# Revit family: IS_Douro_R3806_BIM_NL
name_source: partatom
category: Plumbing Fixtures
revit_build: Autodesk Revit MEP 2014 (Build: 20130308_1515(x64)
units: mm (PartAtom-declared; Revit-internal decimal feet)

## types (1)
- R380601 - DUORO UITGIETBAK WIT
    Accessories = www.idealstandardnederland.nl
    AreaUnits = millimeters
    Assembly Code = C1030200
    AssetType = Vast
    BIMObjectName = ISI_IdealStandard_JanitorialSinks_R380601
    BarCode = 3139000034436
    Brand = Ideal Standard
    CWFU = 0
    Color = Wit
    ConnectionType = Sanitair
    Cost = 0 $
    Default Elevation = 803 mm  [stored 2.63451 ft]
    Description = Contour 21 / Douro uitgietbak 445 mm van keramiek met stootrand. Te monteren met rooster (R6378AA). Rooster en bevestigingsset separaat te bestellen.
    DrainSize = 0 mm  [stored 0 ft]
    DurationUnit = jaar
    ECA = No
    ExpectedLife = 25
    Features = Uitgietbak 445 mm van keramiek met stootrand. Te monteren met rooster (R6378AA). Rooster en bevestigingsset separaat te bestellen.
    Finish = Wit
    HWFU = 0
    IfcExportAs = IfcSanitaryTerminalType
    IfcExportType = SINK
    InstallationInstructions = http://www.idealstandardnederland.nl
    LinearUnits = millimeters
    ManufacturerURL = www.idealstandardnederland.nl
    Material = Keramiek
    MetalFinish = ASH_ArmitageShanks_StainlessSteel_Silver_Render
    Model = R380601
    ModelNumber = R380601
    ModelReference = Contour 21 / Douro uitgietbak 445 mm van keramiek met stootrand. Te monteren met rooster (R6378AA). Rooster en bevestigingsset separaat te bestellen.
    NBSDescription = Janitorial units
    NBSReference = 45-35-70/401
    Name = JanitorialSinks_R380601_IdealStandard
    NettWeight = 17.204 kg
    NominalDepth = 0 mm  [stored 0 ft]
    NominalHeight = 345 mm  [stored 1.13189 ft]
    NominalLength = 354 mm
    NominalWidth = 445 mm
    ProductInformation = http://www.idealstandardnederland.nl
    Shape = Gesculptuurd
    SinkMounting = Wall
    SinkType = Other
    Size = 445 x 354 x 345 mm
    Space = Internal
    URL = www.idealstandardnederland.nl
    Uniclass2015Code = Pr_40_20_96_44
    Uniclass2015Title = Janitorial sinks
    Uniclass2015Version = Products v1.1
    Version = 1
    VolumeUnits = liter
    WFU = 0
    WRAS = No
    WarrantyDescription = Fabrieksgarantie
    WarrantyDurationParts = 5
    WarrantyDurationUnit = jaar
    WaterEfficientProduct = No

note: [stored X ft] marks values corroborated as IEEE doubles in the binary element streams (Revit-internal decimal feet)

## geometry (parser evidence)
native form markers: Blend x2, Sweep x1
no freeform markers — native parametric forms only
